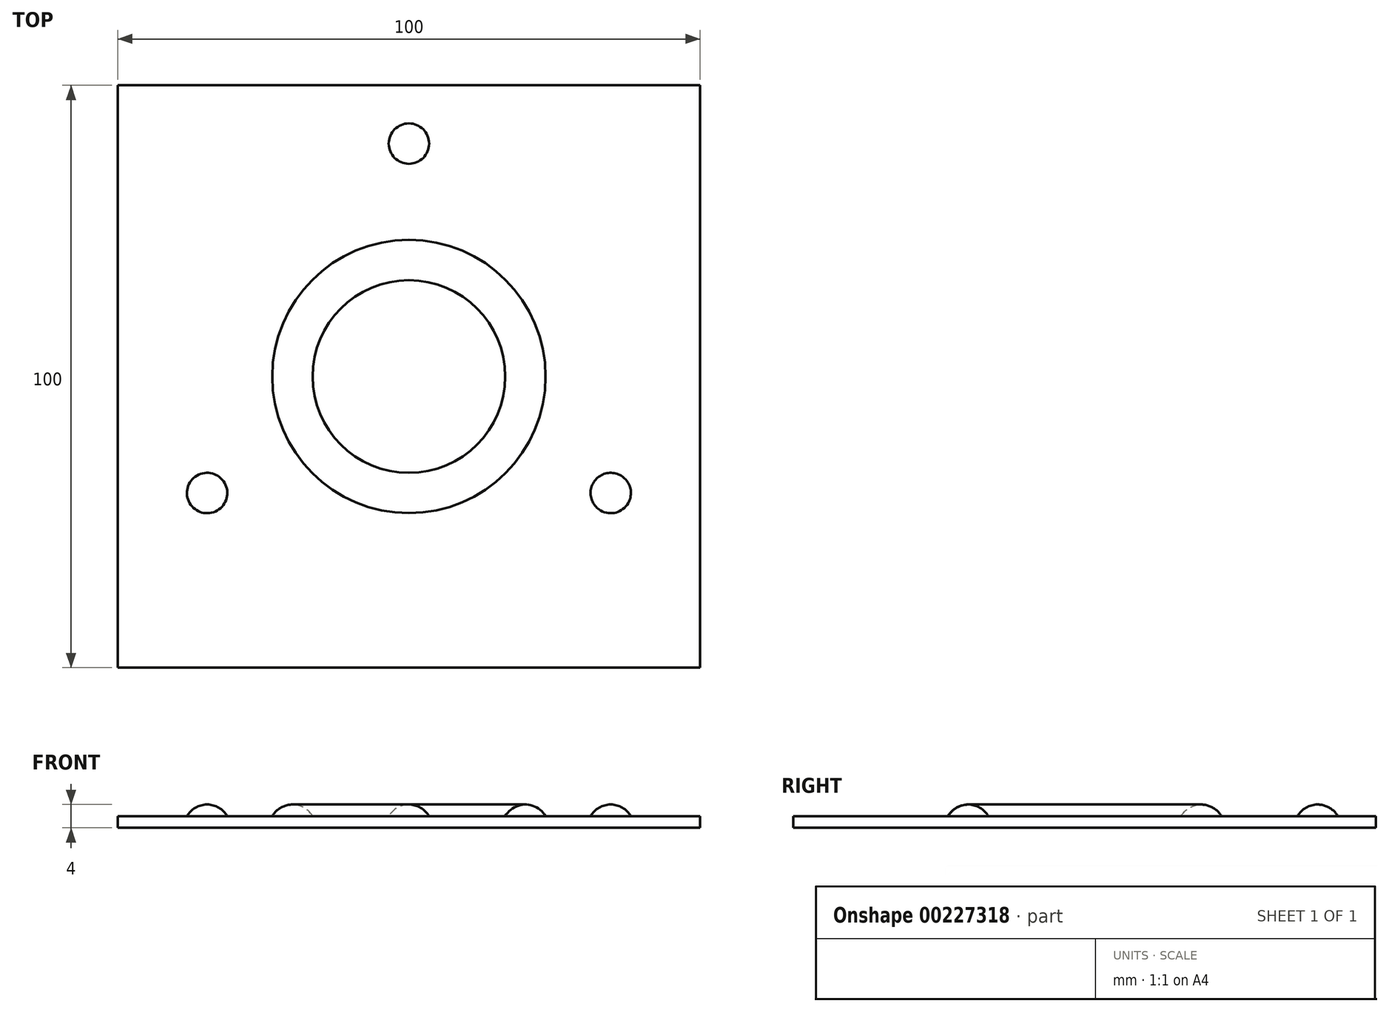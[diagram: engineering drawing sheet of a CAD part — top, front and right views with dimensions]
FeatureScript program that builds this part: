
annotation { "Feature Type Name" : "Feature", "Feature Type Description" : "" }
export const myFeature = defineFeature(function(context is Context, id is Id, definition is map)
    precondition{}
    {
        {
            var Q0;
            Q0=qCreatedBy(makeId("Top.planeOp"),FACE);
            var sketch = newSketch(context, id + "F0", { "sketchPlane" : qUnion([Q0])});
            skLineSegment(sketch, "E0.bottom", {"start": v(-50, -50) * mm, "end": v(50, -50) * mm});
            skLineSegment(sketch, "E0.top", {"start": v(-50, 50) * mm, "end": v(50, 50) * mm});
            skLineSegment(sketch, "E0.left", {"start": v(-50, -50) * mm, "end": v(-50, 50) * mm});
            skLineSegment(sketch, "E0.right", {"start": v(50, -50) * mm, "end": v(50, 50) * mm});
            skSolve(sketch);
        }
        {
            var Q0;
            Q0 = qSketchRegion(id + "F0", true);
            extrude(context, id + "F1", {"entities" : qUnion([Q0]), "depth" : 2 * mm});
        }
        {
            var Q0;
            Q0=qCreatedBy(makeId("Right.planeOp"),FACE);
            var sketch = newSketch(context, id + "F2", { "sketchPlane" : qUnion([Q0])});
            skArc(sketch, "E1", {"start": v(24, 0) * mm, "mid": v(20, 4) * mm, "end": v(16, 0) * mm});
            skLineSegment(sketch, "E2", {"start": v(16, 0) * mm, "end": v(24, 0) * mm});
            skLineSegment(sketch, "E3", {"start": v(0, 35.63) * mm, "end": v(0, -28.08) * mm, "construction": true});
            skSolve(sketch);
        }
        {
            var Q0;
            Q0 = qSketchRegion(id + "F2", true);
            var Q1;
            Q1=sQuery(id+"F2.wireOp",EDGE,"E3");
            revolve(context, id + "F3", {"operationType" : NewBodyOperationType.ADD, "entities" : qUnion([Q0]), "axis" : qUnion([Q1]), "revolveType" : RevolveType.FULL});
        }
        {
            var Q0;
            Q0=qCreatedBy(makeId("Right.planeOp"),FACE);
            var sketch = newSketch(context, id + "F4", { "sketchPlane" : qUnion([Q0])});
            skLineSegment(sketch, "E4", {"start": v(40, 18.37) * mm, "end": v(40, -15.43) * mm, "construction": true});
            skArc(sketch, "E5", {"start": v(44, 0) * mm, "mid": v(42.83, 2.83) * mm, "end": v(40, 4) * mm});
            skPoint(sketch, "E5.centerSnap0", {"position": v(40, 1.47) * mm});
            skLineSegment(sketch, "E6", {"start": v(40, 0) * mm, "end": v(44, 0) * mm});
            skLineSegment(sketch, "E7", {"start": v(40, 0) * mm, "end": v(40, 4) * mm});
            skSolve(sketch);
        }
        {
            var Q0;
            Q0 = qSketchRegion(id + "F4", true);
            var Q1;
            Q1=sQuery(id+"F4.wireOp",EDGE,"E4");
            revolve(context, id + "F5", {"operationType" : NewBodyOperationType.ADD, "entities" : qUnion([Q0]), "axis" : qUnion([Q1]), "revolveType" : RevolveType.FULL});
        }
        {
            var Q0;
            Q0=makeQuery(id+"F5.opRevolve","SWEPT_FACE",FACE,{"disambiguationData":[OSD([sQuery(id+"F4.wireOp",EDGE,"E5")])]});
            var Q1;
            Q1=sQuery(id+"F2.wireOp",EDGE,"E3");
            circularPattern(context, id + "F6", {"patternType" : PatternType.FACE, "faces" : qUnion([Q0]), "axis" : qUnion([Q1]), "angle" : 360 * degree, "instanceCount" : 3, "equalSpace" : true});
        }
    });
